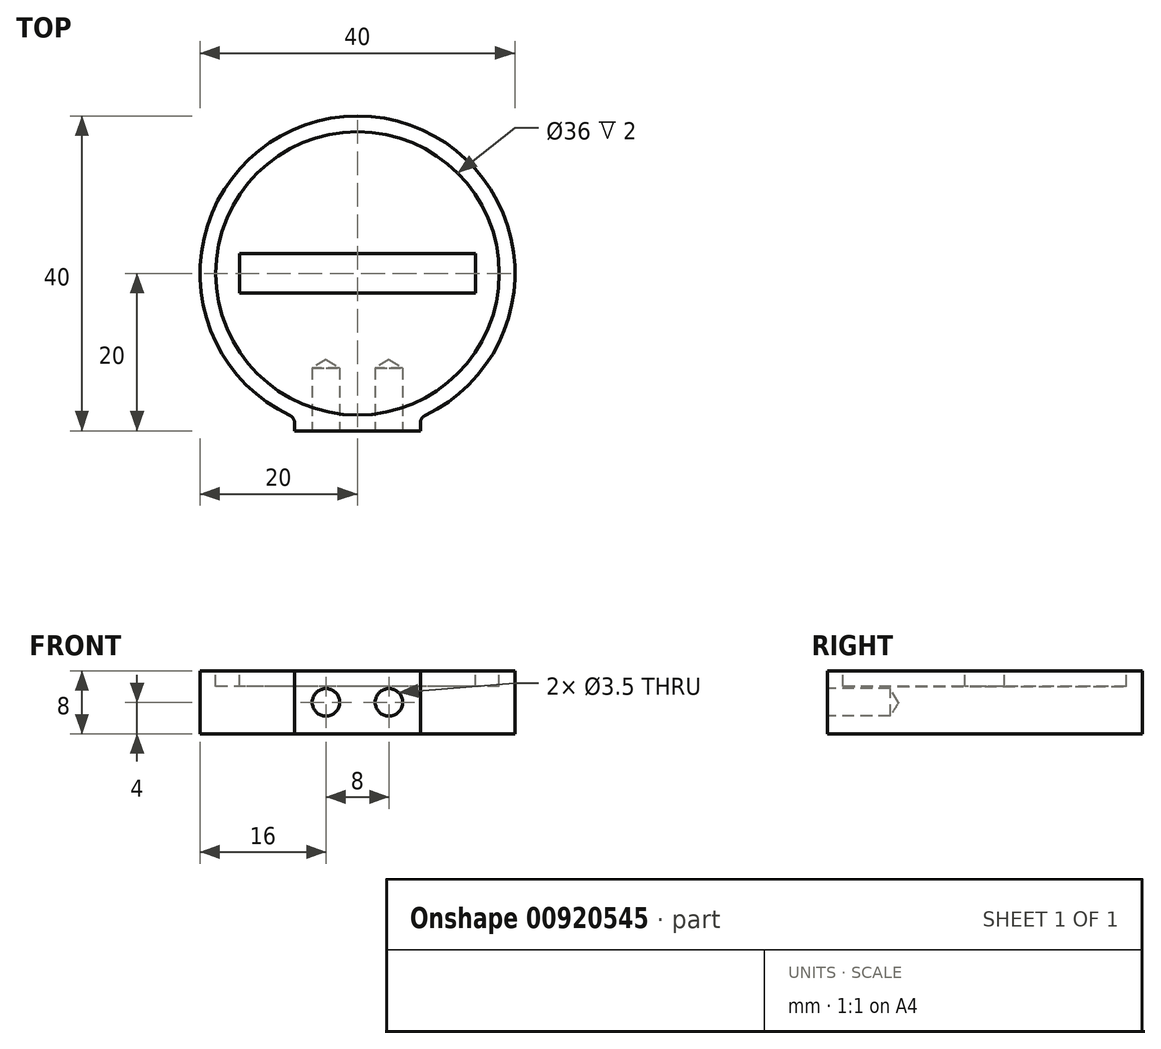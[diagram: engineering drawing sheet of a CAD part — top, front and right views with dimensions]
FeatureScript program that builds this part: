
annotation { "Feature Type Name" : "Feature", "Feature Type Description" : "" }
export const myFeature = defineFeature(function(context is Context, id is Id, definition is map)
    precondition{}
    {
        {
            var Q0;
            Q0=qCreatedBy(makeId("Top.planeOp"),FACE);
            var sketch = newSketch(context, id + "F0", { "sketchPlane" : qUnion([Q0])});
            skCircle(sketch, "E0", {"center": v(0, 0) * mm, "radius": 20 * mm});
            skSolve(sketch);
        }
        {
            var Q0;
            Q0=makeQuery(id+"F0.imprint","IMPRINT",FACE,{"disambiguationData":[TD([[makeQuery(id+"F0.imprint","IMPRINT",EDGE,{"derivedFrom":sQuery(id+"F0.wireOp",EDGE,"E0")}),1.0]])]});
            extrude(context, id + "F1", {"entities" : qUnion([Q0]), "depth" : 8 * mm, "offsetDistance" : 25 * mm});
        }
        {
            var Q0;
            Q0=makeQuery(id+"F1.opExtrude","CAP_FACE",FACE,{"disambiguationData":[OSD([sQuery(id+"F0.wireOp",EDGE,"E0")])],"isStart":false});
            var sketch = newSketch(context, id + "F2", { "sketchPlane" : qUnion([Q0])});
            skCircle(sketch, "E1", {"center": v(0, 0) * mm, "radius": 18 * mm});
            skLineSegment(sketch, "E2.bottom", {"start": v(15, 2.5) * mm, "end": v(-15, 2.5) * mm});
            skLineSegment(sketch, "E2.top", {"start": v(15, -2.5) * mm, "end": v(-15, -2.5) * mm});
            skLineSegment(sketch, "E2.left", {"start": v(15, 2.5) * mm, "end": v(15, -2.5) * mm});
            skLineSegment(sketch, "E2.right", {"start": v(-15, 2.5) * mm, "end": v(-15, -2.5) * mm});
            skSolve(sketch);
        }
        {
            var Q0;
            Q0=makeQuery(id+"F2.imprint","IMPRINT",FACE,{"disambiguationData":[TD([[makeQuery(id+"F2.imprint","IMPRINT",EDGE,{"derivedFrom":sQuery(id+"F2.wireOp",EDGE,"E1")}),1.0]])]});
            extrude(context, id + "F3", {"entities" : qUnion([Q0]), "operationType" : NewBodyOperationType.REMOVE, "oppositeDirection" : true, "depth" : 2 * mm, "offsetDistance" : 25 * mm});
        }
        {
            var Q0;
            Q0=qCreatedBy(makeId("Front.planeOp"),FACE);
            cPlane(context, id + "F4", {"entities" : qUnion([Q0]), "cplaneType" : CPlaneType.OFFSET, "offset" : 20 * mm, "width" : 150 * mm, "height" : 150 * mm});
        }
        {
            var Q0;
            Q0=qCreatedBy(id+"F4.planeOp",FACE);
            var sketch = newSketch(context, id + "F5", { "sketchPlane" : qUnion([Q0])});
            skLineSegment(sketch, "E3.bottom", {"start": v(-8, 0) * mm, "end": v(8, 0) * mm});
            skLineSegment(sketch, "E3.top", {"start": v(-8, 8) * mm, "end": v(8, 8) * mm});
            skLineSegment(sketch, "E3.left", {"start": v(-8, 0) * mm, "end": v(-8, 8) * mm});
            skLineSegment(sketch, "E3.right", {"start": v(8, 0) * mm, "end": v(8, 8) * mm});
            skPoint(sketch, "E4", {"position": v(-4, 4) * mm});
            skPoint(sketch, "E5.MirrorP", {"position": v(4, 4) * mm});
            skSolve(sketch);
        }
        {
            var Q0;
            Q0=makeQuery(id+"F5.imprint","IMPRINT",FACE,{"disambiguationData":[TD([[makeQuery(id+"F5.imprint","IMPRINT",EDGE,{"derivedFrom":sQuery(id+"F5.wireOp",EDGE,"E3.bottom")}),1.0]])]});
            var Q1;
            Q1=makeQuery(id+"F3.boolean.opBoolean","COPY",FACE,{"derivedFrom":makeQuery(id+"F3.opExtrude","SWEPT_FACE",FACE,{"disambiguationData":[OSD([sQuery(id+"F2.wireOp",EDGE,"E1")])]})});
            extrude(context, id + "F6", {"entities" : qUnion([Q0]), "operationType" : NewBodyOperationType.ADD, "endBound" : BoundingType.UP_TO_SURFACE, "oppositeDirection" : true, "depth" : 25 * mm, "endBoundEntityFace" : qUnion([Q1]), "offsetDistance" : 25 * mm});
        }
        {
            var Q0;
            Q0=sQuery(id+"F5.wireOp",VERTEX,"E5.MirrorP");
            var Q1;
            Q1=sQuery(id+"F5.wireOp",VERTEX,"E4");
            var Q2;
            Q2=makeQuery(id+"F1.opExtrude","SWEPT_BODY",BODY,{"disambiguationData":[OSD([sQuery(id+"F0.wireOp",EDGE,"E0")])]});
            hole(context, id + "F7", {"style" : HoleStyle.SIMPLE, "endStyle" : HoleEndStyle.BLIND, "holeDiameter" : 3.5 * mm, "majorDiameter" : 5 * mm, "holeDepth" : 8 * mm, "isTappedThrough" : true, "tappedDepth" : 12 * mm, "tapClearance" : 3, "locations" : qUnion([Q0, Q1]), "scope" : qUnion([Q2])});
        }
        {
            var Q0;
            Q0=makeQuery(id+"F6.boolean.opBoolean","INTERSECT",EDGE,{"derivedFrom":[makeQuery(id+"F1.opExtrude","SWEPT_FACE",FACE,{"disambiguationData":[OSD([sQuery(id+"F0.wireOp",EDGE,"E0")])]}),makeQuery(id+"F6.opExtrude","SWEPT_FACE",FACE,{"disambiguationData":[OSD([sQuery(id+"F5.wireOp",EDGE,"E3.right")])]})]});
            var Q1;
            Q1=makeQuery(id+"F6.boolean.opBoolean","INTERSECT",EDGE,{"derivedFrom":[makeQuery(id+"F1.opExtrude","SWEPT_FACE",FACE,{"disambiguationData":[OSD([sQuery(id+"F0.wireOp",EDGE,"E0")])]}),makeQuery(id+"F6.opExtrude","SWEPT_FACE",FACE,{"disambiguationData":[OSD([sQuery(id+"F5.wireOp",EDGE,"E3.left")])]})]});
            fillet(context, id + "F8", {"entities" : qUnion([Q0, Q1]), "radius" : 1 * mm, "tangentPropagation" : true, "allowEdgeOverflow" : false});
        }
    });
